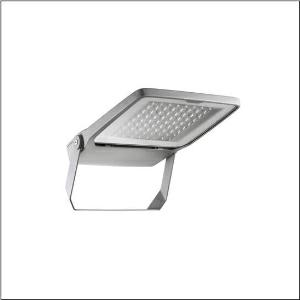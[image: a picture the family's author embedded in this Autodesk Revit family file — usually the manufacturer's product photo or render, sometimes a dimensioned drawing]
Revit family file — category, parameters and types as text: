
# Revit family: floodlight_fl_20_mini___pl52_5xa7672b2d1ac_d8cf
name_source: partatom
category: Lighting Fixtures
units: mm (PartAtom-declared; Revit-internal decimal feet)

## family parameters
Cut with Voids When Loaded = No
Host = Face
Light Source = No
Part Type = Normal
Room Calculation Point = No
Round Connector Dimension = Use Diameter
Shared = No

## types (1)
- --- (1 x LED 4000K / CRI = 70 (unbekannt), 6270 lm, 4000K)
    Apparent Load = 51 VA
    CIE Flux Codes = 27 59 98 100 100
    Color Rendering = 70
    Color Temperature = 4000K
    Default Elevation = 1800 mm
    Description = Floodlight FL 20 mini, floodlight, primary light control with lens, of plastic, primary optical cover: protective disc, of toughened safety glass, transparent, light distribution: PL52, light emission: direct distribution, primary light characteristic: asymmetric, installation type: surface-mounted, LED, High Power LED, rated luminous flux: 6.270lm, luminous efficacy: 123lm/W, light colour: 740, colour temperature: 4000K, control gear: ECG Plus, control: flexible luminous flux parameterisation, time-dependent luminous flux control, digital communication interface, power reduction, overheat protection, electronic power reduction, with terminal, 5-pole, max. 2.5mm², mains connection: 220..240V, AC, 50/60Hz, rated input power: 51W, LED unit, of diecast aluminium, powder-coated, Siteco® metallic grey (DB 702S), corrosivity category C5 mid according to DIN EN ISO 12944, incl. 1x M20 cable gland for cable Ø 6.5..12mm, length: 446mm, width: 355mm, height: 62mm, housing frame, of diecast aluminium, powder-coated, Siteco® metallic grey (DB 702S), mounting bracket, of steel, powder-coated, Siteco® metallic grey (DB 702S), DALI, protection rating (complete): IP66, insulation class (complete): insulation class II (safety insulation), certification: CE, ENEC, VDE, protection symbol: D, permissible operating ambient temperature: -40..+40°C, permissible operating ambient temperature for outdoor applications: -40..+50°C, standard: DIN EN 12944, packaging unit: 1 piece

Light Distribution: PL52
    Height = 62 mm  [stored 0.203412 ft]
    Lamp = 1 x LED 4000K / CRI >= 70 (unbekannt)
    Lamp Light Flux = 6270 lm
    Lamp count = 1
    Length = 467 mm
    Luminous efficacy = 123 lm/W
    Manufacturer = Siteco
    ModVariant = No
    Model = 5XA7672B2D1AC
    Mounting Place = Wall
    Mounting Type = Surface mounted
    Number of Poles = 1
    OnlyDefault = Yes
    Power Factor = 1
    Product Name = Floodlight FL 20 mini | PL52
    Product group = floodlight | wall mounted
    ProductGroupID = 2001
    Protection Class = Protection class II
    Protection Degree = IP 66
    RLX_Detail_Level = 1
    RLX_Emergency_Light_Flux = 0 lm
    RLX_Emergency_Type = 0
    RLX_Emergency_Type_DB = No
    RlxData = <blob elided: 74369 chars, md5=c51540f0>
    Socket = socket
    Standby Power = 0 W
    System Light Flux = 6270 lm
    System Power = 51 W
    Type Comments = factory setting: luminous flux: 100 % | dim-lin: 254 | 520 mA
    Type Image = l_1005948.jpg
    URL = http://relux.com
    VarID = @adj_163957
    Voltage = 0 V
    Weight = 0.00 kg
    Width = 335 mm

note: [stored X ft] marks values corroborated as IEEE doubles in the binary element streams (Revit-internal decimal feet)

## geometry (parser evidence)
native form markers: Blend x4, Sweep x14
no freeform markers — native parametric forms only
